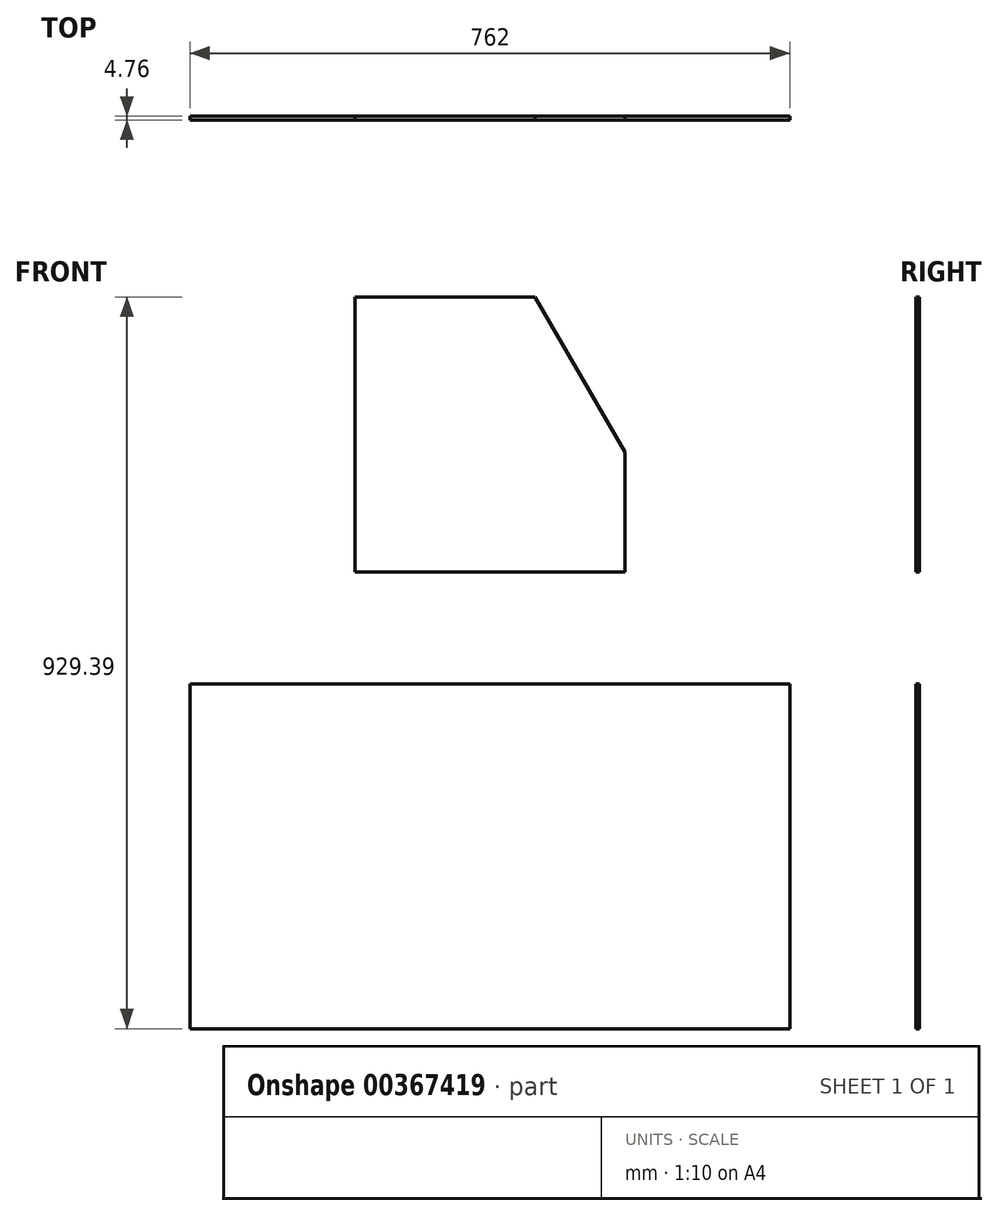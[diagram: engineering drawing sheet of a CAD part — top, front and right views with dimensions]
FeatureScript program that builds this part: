
annotation { "Feature Type Name" : "Feature", "Feature Type Description" : "" }
export const myFeature = defineFeature(function(context is Context, id is Id, definition is map)
    precondition{}
    {
        {
            var Q0;
            Q0=qCreatedBy(makeId("Front.planeOp"),FACE);
            var sketch = newSketch(context, id + "F0", { "sketchPlane" : qUnion([Q0])});
            skLineSegment(sketch, "E0.bottom", {"start": v(381, 219.08) * mm, "end": v(-381, 219.08) * mm});
            skLineSegment(sketch, "E0.top", {"start": v(381, -219.08) * mm, "end": v(-381, -219.08) * mm});
            skLineSegment(sketch, "E0.left", {"start": v(381, 219.08) * mm, "end": v(381, -219.08) * mm});
            skLineSegment(sketch, "E0.right", {"start": v(-381, 219.08) * mm, "end": v(-381, -219.08) * mm});
            skPoint(sketch, "E0.middle", {"position": v(0, 0) * mm});
            skSolve(sketch);
        }
        {
            var Q0;
            Q0 = qSketchRegion(id + "F0", true);
            extrude(context, id + "F1", {"entities" : qUnion([Q0]), "depth" : 4.76 * mm});
        }
        {
            var Q0;
            Q0=qCreatedBy(makeId("Front.planeOp"),FACE);
            var sketch = newSketch(context, id + "F2", { "sketchPlane" : qUnion([Q0])});
            skLineSegment(sketch, "E1.bottom", {"start": v(171.45, 361.07) * mm, "end": v(-171.45, 361.07) * mm});
            skLineSegment(sketch, "E1.top", {"start": v(171.45, 710.32) * mm, "end": v(-171.45, 710.32) * mm});
            skLineSegment(sketch, "E1.left", {"start": v(171.45, 361.07) * mm, "end": v(171.45, 710.32) * mm});
            skLineSegment(sketch, "E1.right", {"start": v(-171.45, 361.07) * mm, "end": v(-171.45, 710.32) * mm});
            skPoint(sketch, "E1.middle", {"position": v(0, 535.7) * mm});
            skSolve(sketch);
        }
        {
            var Q0;
            Q0 = qSketchRegion(id + "F2", true);
            extrude(context, id + "F3", {"entities" : qUnion([Q0]), "depth" : 4.76 * mm});
        }
        {
            var Q0;
            Q0=makeQuery(id+"F3.opExtrude","CAP_FACE",FACE,{"disambiguationData":[OSD([sQuery(id+"F2.wireOp",EDGE,"E1.bottom"),sQuery(id+"F2.wireOp",EDGE,"E1.top"),sQuery(id+"F2.wireOp",EDGE,"E1.left"),sQuery(id+"F2.wireOp",EDGE,"E1.right")])],"isStart":false});
            var sketch = newSketch(context, id + "F4", { "sketchPlane" : qUnion([Q0])});
            skLineSegment(sketch, "E2", {"start": v(171.45, 513.47) * mm, "end": v(57.15, 710.32) * mm});
            skLineSegment(sketch, "E3", {"start": v(57.15, 710.32) * mm, "end": v(171.45, 710.32) * mm});
            skLineSegment(sketch, "E4", {"start": v(171.45, 710.32) * mm, "end": v(171.45, 513.47) * mm});
            skSolve(sketch);
        }
        {
            var Q0;
            Q0 = qSketchRegion(id + "F4", true);
            extrude(context, id + "F5", {"entities" : qUnion([Q0]), "operationType" : NewBodyOperationType.REMOVE, "endBound" : BoundingType.UP_TO_NEXT, "oppositeDirection" : true, "depth" : 25.4 * mm});
        }
    });
